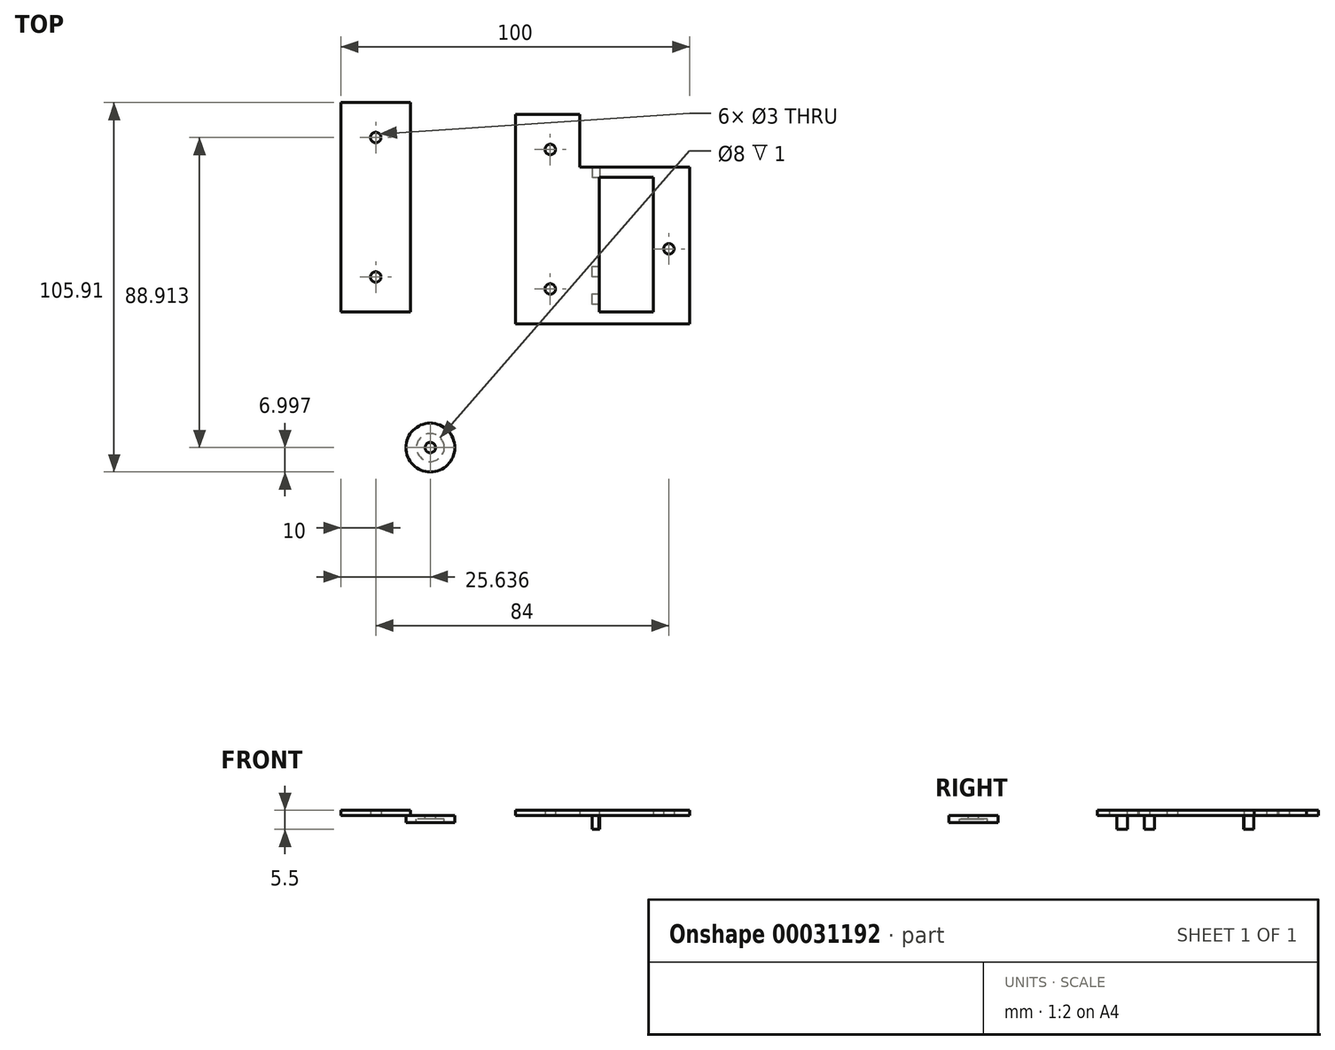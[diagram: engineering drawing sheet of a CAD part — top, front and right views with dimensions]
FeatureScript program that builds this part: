
annotation { "Feature Type Name" : "Feature", "Feature Type Description" : "" }
export const myFeature = defineFeature(function(context is Context, id is Id, definition is map)
    precondition{}
    {
        {
            var Q0;
            Q0=qCreatedBy(makeId("Top.planeOp"),FACE);
            var sketch = newSketch(context, id + "F0", { "sketchPlane" : qUnion([Q0])});
            skLineSegment(sketch, "E0", {"start": v(-10, -3.44) * mm, "end": v(40, -3.44) * mm});
            skLineSegment(sketch, "E1", {"start": v(40, 41.56) * mm, "end": v(8.5, 41.56) * mm});
            skLineSegment(sketch, "E2", {"start": v(8.5, 41.56) * mm, "end": v(8.5, 56.56) * mm});
            skLineSegment(sketch, "E3", {"start": v(8.5, 56.56) * mm, "end": v(-10, 56.56) * mm});
            skCircle(sketch, "E4", {"center": v(0, 46.56) * mm, "radius": 1.5 * mm});
            skCircle(sketch, "E5", {"center": v(0, 6.56) * mm, "radius": 1.5 * mm});
            skCircle(sketch, "E6", {"center": v(34, 18.06) * mm, "radius": 1.5 * mm});
            skLineSegment(sketch, "E7", {"start": v(-10, 56.56) * mm, "end": v(-10, -3.44) * mm});
            skLineSegment(sketch, "E8", {"start": v(40, 41.56) * mm, "end": v(40, -3.44) * mm});
            skPoint(sketch, "E9.start.orphan", {"position": v(-14.5, 56.56) * mm});
            skLineSegment(sketch, "E10.bottom", {"start": v(14, 38.56) * mm, "end": v(29.5, 38.56) * mm});
            skLineSegment(sketch, "E10.top", {"start": v(14, 0) * mm, "end": v(29.5, 0) * mm});
            skLineSegment(sketch, "E10.left", {"start": v(14, 38.56) * mm, "end": v(14, 0) * mm});
            skLineSegment(sketch, "E10.right", {"start": v(29.5, 38.56) * mm, "end": v(29.5, 0) * mm});
            skSolve(sketch);
        }
        {
            var Q0;
            Q0=qCreatedBy(makeId("Top.planeOp"),FACE);
            var sketch = newSketch(context, id + "F1", { "sketchPlane" : qUnion([Q0])});
            skLineSegment(sketch, "E11.bottom", {"start": v(-60, 60) * mm, "end": v(-40, 60) * mm});
            skLineSegment(sketch, "E11.top", {"start": v(-60, 0) * mm, "end": v(-40, 0) * mm});
            skLineSegment(sketch, "E11.left", {"start": v(-60, 60) * mm, "end": v(-60, 0) * mm});
            skLineSegment(sketch, "E11.right", {"start": v(-40, 60) * mm, "end": v(-40, 0) * mm});
            skCircle(sketch, "E12", {"center": v(-50, 50) * mm, "radius": 1.5 * mm});
            skCircle(sketch, "E13", {"center": v(-50, 10) * mm, "radius": 1.5 * mm});
            skSolve(sketch);
        }
        {
            var Q0;
            Q0=makeQuery(id+"F1.imprint","IMPRINT",FACE,{"disambiguationData":[TD([[makeQuery(id+"F1.imprint","IMPRINT",EDGE,{"derivedFrom":sQuery(id+"F1.wireOp",EDGE,"E11.bottom")}),-1.0]])]});
            extrude(context, id + "F2", {"entities" : qUnion([Q0]), "depth" : 1.5 * mm});
        }
        {
            var Q0;
            Q0 = qSketchRegion(id + "F0", true);
            extrude(context, id + "F3", {"entities" : qUnion([Q0]), "depth" : 1.5 * mm});
        }
        {
            var Q0;
            Q0=makeQuery(id+"F0.imprint","IMPRINT",FACE,{"disambiguationData":[TD([[makeQuery(id+"F0.imprint","IMPRINT",EDGE,{"derivedFrom":sQuery(id+"F0.wireOp",EDGE,"E0")}),1.0]])]});
            var sketch = newSketch(context, id + "F4", { "sketchPlane" : qUnion([Q0])});
            skLineSegment(sketch, "E14.0", {"start": v(14, 13) * mm, "end": v(14, 10) * mm});
            skLineSegment(sketch, "E15", {"start": v(14, 10) * mm, "end": v(12, 10) * mm});
            skLineSegment(sketch, "E16", {"start": v(12, 10) * mm, "end": v(12, 13) * mm});
            skLineSegment(sketch, "E17", {"start": v(12, 13) * mm, "end": v(14, 13) * mm});
            skPoint(sketch, "E18.orphan", {"position": v(14, 0) * mm});
            skPoint(sketch, "E19.orphan", {"position": v(14, 38.56) * mm});
            skLineSegment(sketch, "E20", {"start": v(14.16, 38.44) * mm, "end": v(12.16, 38.44) * mm});
            skLineSegment(sketch, "E21", {"start": v(12.16, 38.44) * mm, "end": v(12.16, 41.44) * mm});
            skLineSegment(sketch, "E22", {"start": v(12.16, 41.44) * mm, "end": v(14.16, 41.44) * mm});
            skLineSegment(sketch, "E23.trimOffspring", {"start": v(14.16, 41.44) * mm, "end": v(14.16, 38.44) * mm});
            skLineSegment(sketch, "E24", {"start": v(13.97, 2.15) * mm, "end": v(11.97, 2.15) * mm});
            skLineSegment(sketch, "E25", {"start": v(11.97, 2.15) * mm, "end": v(11.97, 5.15) * mm});
            skLineSegment(sketch, "E26", {"start": v(11.97, 5.15) * mm, "end": v(13.97, 5.15) * mm});
            skLineSegment(sketch, "E27.trimOffspring", {"start": v(13.97, 5.15) * mm, "end": v(13.97, 2.15) * mm});
            skSolve(sketch);
        }
        {
            var Q0;
            Q0=makeQuery(id+"F4.imprint","IMPRINT",FACE,{"disambiguationData":[TD([[makeQuery(id+"F4.imprint","IMPRINT",EDGE,{"derivedFrom":sQuery(id+"F4.wireOp",EDGE,"E15")}),-1.0]])]});
            var Q1;
            Q1=makeQuery(id+"F4.imprint","IMPRINT",FACE,{"disambiguationData":[TD([[makeQuery(id+"F4.imprint","IMPRINT",EDGE,{"derivedFrom":sQuery(id+"F4.wireOp",EDGE,"2be85b80-0c06-4663-ae8b-0d4c67dfcaf4.0")}),-1.0]])]});
            var Q2;
            Q2=makeQuery(id+"F4.imprint","IMPRINT",FACE,{"disambiguationData":[TD([[makeQuery(id+"F4.imprint","IMPRINT",EDGE,{"derivedFrom":sQuery(id+"F4.wireOp",EDGE,"E24")}),-1.0]])]});
            var Q3;
            {var subQ4=sQuery(id+"F4.wireOp",EDGE,"E21");Q3=makeQuery(id+"F4.imprint","IMPRINT",FACE,{"disambiguationData":[TD([[makeQuery(id+"F4.imprint","IMPRINT",EDGE,{"derivedFrom":subQ4}),-1.0]])]});}
            extrude(context, id + "F5", {"entities" : qUnion([Q0, Q1, Q2, Q3]), "operationType" : NewBodyOperationType.ADD, "oppositeDirection" : true, "depth" : 4 * mm});
        }
        {
            var Q0;
            Q0=qCreatedBy(makeId("Top.planeOp"),FACE);
            var sketch = newSketch(context, id + "F6", { "sketchPlane" : qUnion([Q0])});
            skCircle(sketch, "E28", {"center": v(-34.36, -38.91) * mm, "radius": 7 * mm});
            skCircle(sketch, "E29", {"center": v(-34.36, -38.91) * mm, "radius": 1.5 * mm});
            skCircle(sketch, "E30", {"center": v(-34.36, -38.91) * mm, "radius": 4 * mm});
            skSolve(sketch);
        }
        {
            var Q0;
            Q0=makeQuery(id+"F6.imprint","IMPRINT",FACE,{"disambiguationData":[TD([[makeQuery(id+"F6.imprint","IMPRINT",EDGE,{"derivedFrom":sQuery(id+"F6.wireOp",EDGE,"E29")}),-1.0]])]});
            extrude(context, id + "F7", {"entities" : qUnion([Q0]), "oppositeDirection" : true, "depth" : 1 * mm});
        }
        {
            var Q0;
            Q0=makeQuery(id+"F7.opExtrude","SWEPT_BODY",BODY,{"disambiguationData":[OSD([sQuery(id+"F6.wireOp",EDGE,"E29"),sQuery(id+"F6.wireOp",EDGE,"E30")])]});
            deleteBodies(context, id + "F8", {"entities" : qUnion([Q0])});
        }
        {
            var Q0;
            Q0=makeQuery(id+"F6.imprint","IMPRINT",FACE,{"disambiguationData":[TD([[makeQuery(id+"F6.imprint","IMPRINT",EDGE,{"derivedFrom":sQuery(id+"F6.wireOp",EDGE,"E29")}),-1.0]])]});
            extrude(context, id + "F9", {"entities" : qUnion([Q0]), "oppositeDirection" : true, "depth" : 1 * mm});
        }
        {
            var Q0;
            Q0=makeQuery(id+"F6.imprint","IMPRINT",FACE,{"disambiguationData":[TD([[makeQuery(id+"F6.imprint","IMPRINT",EDGE,{"derivedFrom":sQuery(id+"F6.wireOp",EDGE,"E28")}),1.0]])]});
            extrude(context, id + "F10", {"entities" : qUnion([Q0]), "operationType" : NewBodyOperationType.ADD, "oppositeDirection" : true, "depth" : 2 * mm});
        }
    });
